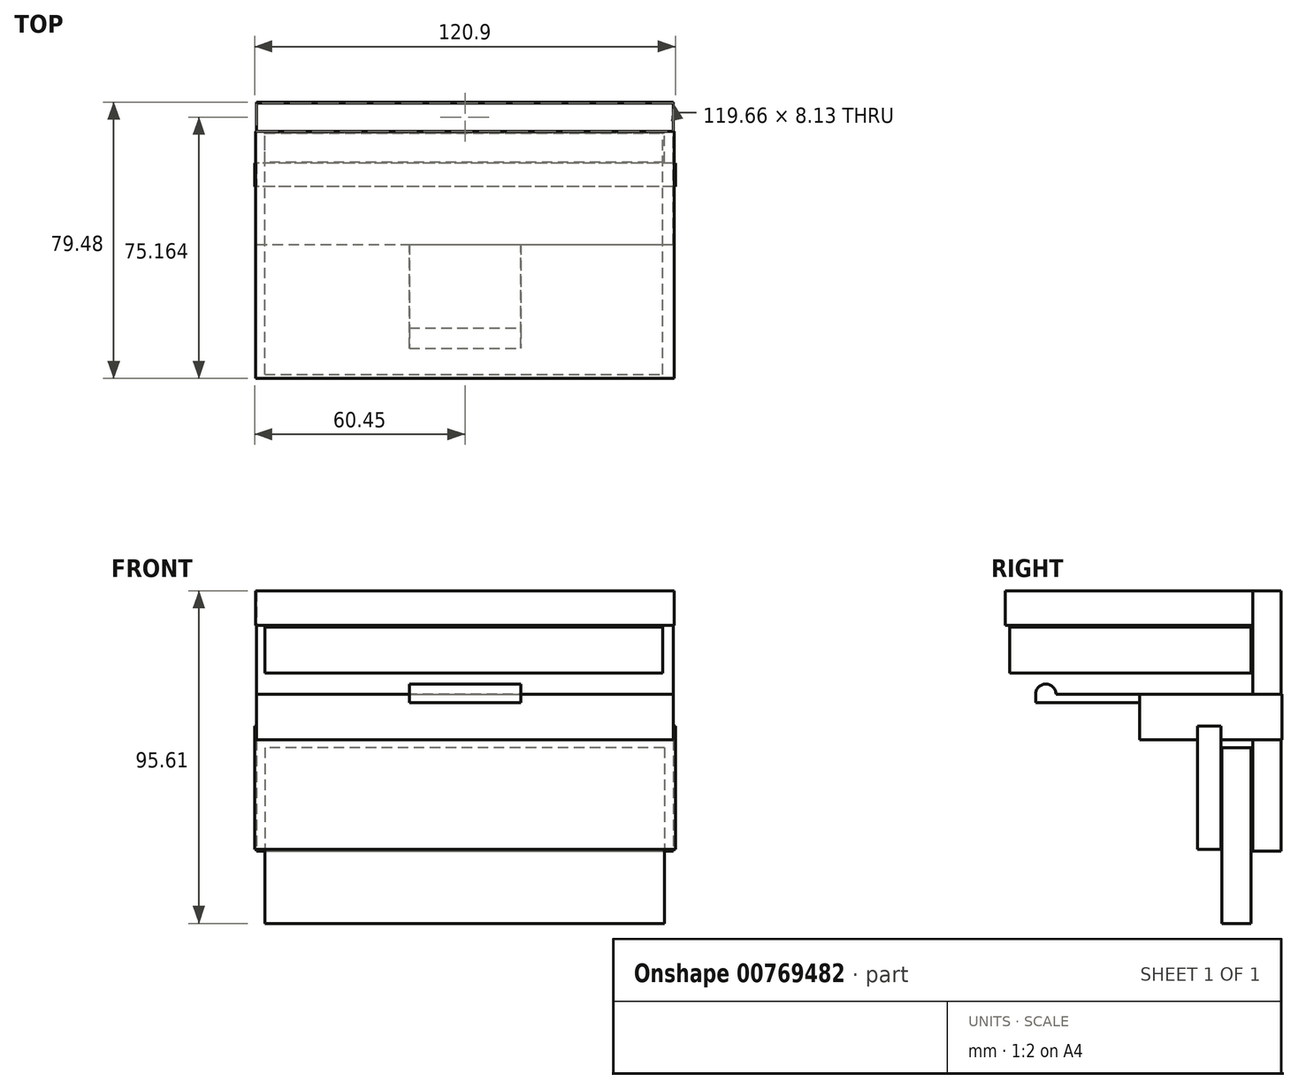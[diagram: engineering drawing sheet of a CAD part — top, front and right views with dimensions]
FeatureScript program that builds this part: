
annotation { "Feature Type Name" : "Feature", "Feature Type Description" : "" }
export const myFeature = defineFeature(function(context is Context, id is Id, definition is map)
    precondition{}
    {
        {
            var Q0;
            Q0=qCreatedBy(makeId("Front.planeOp"),FACE);
            var sketch = newSketch(context, id + "F0", { "sketchPlane" : qUnion([Q0])});
            skLineSegment(sketch, "E0.bottom", {"start": v(-59.83, 37.39) * mm, "end": v(59.83, 37.39) * mm});
            skLineSegment(sketch, "E0.top", {"start": v(-59.83, -37.39) * mm, "end": v(59.83, -37.39) * mm});
            skLineSegment(sketch, "E0.left", {"start": v(-59.83, 37.39) * mm, "end": v(-59.83, -37.39) * mm});
            skLineSegment(sketch, "E0.right", {"start": v(59.83, 37.39) * mm, "end": v(59.83, -37.39) * mm});
            skPoint(sketch, "E0.middle", {"position": v(0, 0) * mm});
            skSolve(sketch);
        }
        {
            var Q0;
            Q0=makeQuery(id+"F0.imprint","IMPRINT",FACE,{"disambiguationData":[TD([[makeQuery(id+"F0.imprint","IMPRINT",EDGE,{"derivedFrom":sQuery(id+"F0.wireOp",EDGE,"E0.bottom")}),-1.0]])]});
            extrude(context, id + "F1", {"entities" : qUnion([Q0]), "oppositeDirection" : true, "depth" : 8.13 * mm, "offsetDistance" : 25.4 * mm});
        }
        {
            var Q0;
            Q0=qCreatedBy(makeId("Front.planeOp"),FACE);
            cPlane(context, id + "F2", {"entities" : qUnion([Q0]), "cplaneType" : CPlaneType.OFFSET, "offset" : 8.38 * mm, "oppositeDirection" : true, "width" : 152.4 * mm, "height" : 152.4 * mm});
        }
        {
            var Q0;
            Q0=qCreatedBy(id+"F2.planeOp",FACE);
            var sketch = newSketch(context, id + "F3", { "sketchPlane" : qUnion([Q0])});
            skLineSegment(sketch, "E1.bottom", {"start": v(-59.86, -5.43) * mm, "end": v(59.86, -5.43) * mm});
            skLineSegment(sketch, "E1.top", {"start": v(-59.86, 7.64) * mm, "end": v(59.86, 7.64) * mm});
            skLineSegment(sketch, "E1.left", {"start": v(-59.86, -5.43) * mm, "end": v(-59.86, 7.64) * mm});
            skLineSegment(sketch, "E1.right", {"start": v(59.86, -5.43) * mm, "end": v(59.86, 7.64) * mm});
            skPoint(sketch, "E1.middle", {"position": v(0, 1.1) * mm});
            skSolve(sketch);
        }
        {
            var Q0;
            Q0 = qSketchRegion(id + "F3", true);
            extrude(context, id + "F4", {"entities" : qUnion([Q0]), "operationType" : NewBodyOperationType.ADD, "depth" : 40.9 * mm, "offsetDistance" : 25.4 * mm});
        }
        {
            var Q0;
            Q0=qCreatedBy(makeId("Right.planeOp"),FACE);
            var sketch = newSketch(context, id + "F5", { "sketchPlane" : qUnion([Q0])});
            skLineSegment(sketch, "E2.bottom", {"start": v(-9.2, -1.46) * mm, "end": v(-15.95, -1.46) * mm});
            skLineSegment(sketch, "E2.top", {"start": v(-9.2, -36.89) * mm, "end": v(-15.95, -36.89) * mm});
            skLineSegment(sketch, "E2.left", {"start": v(-9.2, -1.46) * mm, "end": v(-9.2, -36.89) * mm});
            skLineSegment(sketch, "E2.right", {"start": v(-15.95, -1.46) * mm, "end": v(-15.95, -36.89) * mm});
            skSolve(sketch);
        }
        {
            var Q0;
            Q0 = qSketchRegion(id + "F5", true);
            extrude(context, id + "F6", {"entities" : qUnion([Q0]), "operationType" : NewBodyOperationType.ADD, "depth" : 120.9 * mm, "offsetDistance" : 25.4 * mm, "symmetric" : true});
        }
        {
            var Q0;
            Q0=qCreatedBy(makeId("Top.planeOp"),FACE);
            var sketch = newSketch(context, id + "F7", { "sketchPlane" : qUnion([Q0])});
            skLineSegment(sketch, "E3.bottom", {"start": v(60.13, 0) * mm, "end": v(-60.13, 0) * mm});
            skLineSegment(sketch, "E3.top", {"start": v(60.13, -71.1) * mm, "end": v(-60.13, -71.1) * mm});
            skLineSegment(sketch, "E3.left", {"start": v(60.13, 0) * mm, "end": v(60.13, -71.1) * mm});
            skLineSegment(sketch, "E3.right", {"start": v(-60.13, 0) * mm, "end": v(-60.13, -71.1) * mm});
            skPoint(sketch, "E3.middle", {"position": v(0, -35.55) * mm});
            skSolve(sketch);
        }
        {
            var Q0;
            Q0 = qSketchRegion(id + "F7", true);
            var Q1;
            Q1=makeQuery(id+"F7.imprint","IMPRINT",FACE,{"disambiguationData":[TD([[makeQuery(id+"F7.imprint","IMPRINT",EDGE,{"derivedFrom":sQuery(id+"F7.wireOp",EDGE,"E3.bottom")}),1.0]])]});
            extrude(context, id + "F8", {"entities" : qUnion([Q0, Q1]), "operationType" : NewBodyOperationType.ADD, "depth" : 37.34 * mm, "offsetDistance" : 25.4 * mm, "hasSecondDirection" : true, "secondDirectionOppositeDirection" : false, "secondDirectionDepth" : 27.43 * mm});
        }
        {
            var Q0;
            Q0=qCreatedBy(makeId("Front.planeOp"),FACE);
            var sketch = newSketch(context, id + "F9", { "sketchPlane" : qUnion([Q0])});
            skLineSegment(sketch, "E4.bottom", {"start": v(57.3, -7.7) * mm, "end": v(-57.42, -7.7) * mm});
            skLineSegment(sketch, "E4.top", {"start": v(57.3, -58.22) * mm, "end": v(-57.42, -58.22) * mm});
            skLineSegment(sketch, "E4.left", {"start": v(57.3, -7.7) * mm, "end": v(57.3, -58.22) * mm});
            skLineSegment(sketch, "E4.right", {"start": v(-57.42, -7.7) * mm, "end": v(-57.42, -58.22) * mm});
            skSolve(sketch);
        }
        {
            var Q0;
            Q0 = qSketchRegion(id + "F9", true);
            extrude(context, id + "F10", {"entities" : qUnion([Q0]), "depth" : 8.9 * mm, "offsetDistance" : 25.4 * mm, "hasSecondDirection" : true, "secondDirectionOppositeDirection" : false, "secondDirectionDepth" : 0.5 * mm});
        }
        {
            var Q0;
            Q0=qCreatedBy(makeId("Front.planeOp"),FACE);
            var sketch = newSketch(context, id + "F11", { "sketchPlane" : qUnion([Q0])});
            skLineSegment(sketch, "E5.bottom", {"start": v(-57.52, 26.98) * mm, "end": v(56.8, 26.98) * mm});
            skLineSegment(sketch, "E5.top", {"start": v(-57.52, 13.78) * mm, "end": v(56.8, 13.78) * mm});
            skLineSegment(sketch, "E5.left", {"start": v(-57.52, 26.98) * mm, "end": v(-57.52, 13.78) * mm});
            skLineSegment(sketch, "E5.right", {"start": v(56.8, 26.98) * mm, "end": v(56.8, 13.78) * mm});
            skSolve(sketch);
        }
        {
            var Q0;
            Q0 = qSketchRegion(id + "F11", true);
            extrude(context, id + "F12", {"entities" : qUnion([Q0]), "depth" : 69.85 * mm, "offsetDistance" : 25.4 * mm, "hasSecondDirection" : true, "secondDirectionOppositeDirection" : false, "secondDirectionDepth" : 0.5 * mm});
        }
        {
            var Q0;
            Q0=qCreatedBy(makeId("Right.planeOp"),FACE);
            var sketch = newSketch(context, id + "F13", { "sketchPlane" : qUnion([Q0])});
            skLineSegment(sketch, "E6.0", {"start": v(-32.51, 7.64) * mm, "end": v(8.38, 7.64) * mm});
            skLineSegment(sketch, "E7.0", {"start": v(-32.51, -5.43) * mm, "end": v(-32.51, 7.64) * mm});
            skLineSegment(sketch, "E8", {"start": v(-32.51, 7.64) * mm, "end": v(-62.42, 7.64) * mm});
            skLineSegment(sketch, "E9", {"start": v(-62.42, 7.64) * mm, "end": v(-62.42, 5.17) * mm});
            skLineSegment(sketch, "E10", {"start": v(-62.42, 5.17) * mm, "end": v(-32.51, 5.17) * mm});
            skLineSegment(sketch, "E11", {"start": v(-32.51, 5.17) * mm, "end": v(-32.75, 5.61) * mm});
            skPoint(sketch, "E12", {"position": v(-59.5, 7.64) * mm});
            skArc(sketch, "E13", {"start": v(-62.42, 7.64) * mm, "mid": v(-59.5, 10.56) * mm, "end": v(-56.57, 7.64) * mm});
            skSolve(sketch);
        }
        {
            var Q0;
            Q0 = qSketchRegion(id + "F13", true);
            extrude(context, id + "F14", {"entities" : qUnion([Q0]), "operationType" : NewBodyOperationType.ADD, "oppositeDirection" : true, "depth" : 32 * mm, "offsetDistance" : 25.4 * mm, "hasSecondDirection" : true, "secondDirectionOppositeDirection" : false, "secondDirectionDepth" : 15.75 * mm, "symmetric" : true});
        }
    });
